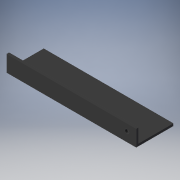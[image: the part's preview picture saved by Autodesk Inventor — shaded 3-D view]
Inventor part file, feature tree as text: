
AUTODESK INVENTOR PART (.ipt)
format: ipt  version: 2018 (Build 220112000, 112)  size: 116,224 bytes
history: native  units: in
note: dims shown in document units (in); Inventor stores cm internally (conversion verified against a paired STEP export)
features: extrude x3, sketch x3, projected_geometry x1
ambient origin geometry x8: Origin, YZ Plane, XZ Plane, XY Plane, X Axis, Y Axis, Z Axis, Center Point
bodies: Solid1 (feature_tree)
feature tree (7):
  extrude  "Extrusion1"  Depth=1.0in
  extrude  "Extrusion2"  Depth=0.0625in
  extrude  "Extrusion3"  Depth=0.375in
  sketch  "Sketch1"  dims[d0=3.5in d1=1.0in]
  sketch  "Sketch2"  dims[d2=0.0625in d3=0.0in d4=0.0625in]
  sketch  "Sketch3"  dims[d5=0.375in d6=0.0in d7=0.25in d8=0.113in d9=0.375in d10=0.0in]
  projected_geometry  "Projected Loop1"
